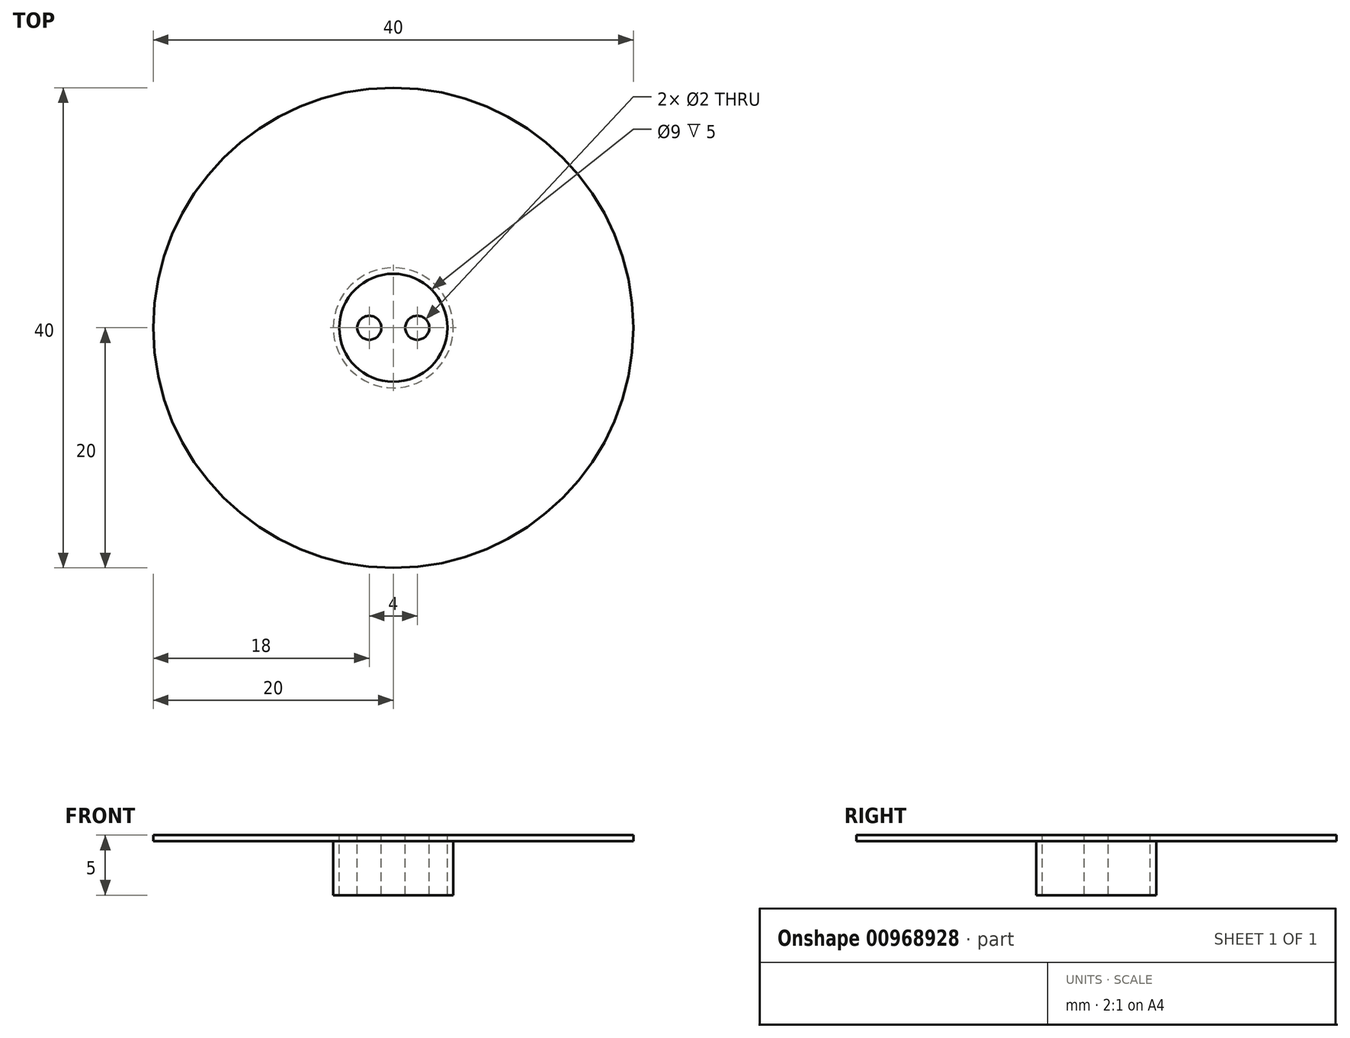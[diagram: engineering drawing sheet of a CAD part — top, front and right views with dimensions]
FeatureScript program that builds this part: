
annotation { "Feature Type Name" : "Feature", "Feature Type Description" : "" }
export const myFeature = defineFeature(function(context is Context, id is Id, definition is map)
    precondition{}
    {
        {
            var Q0;
            Q0=qCreatedBy(makeId("Top.planeOp"),FACE);
            var sketch = newSketch(context, id + "F0", { "sketchPlane" : qUnion([Q0])});
            skCircle(sketch, "E0", {"center": v(0, 0) * mm, "radius": 20 * mm});
            skSolve(sketch);
        }
        {
            var Q0;
            Q0=qSketchRegion(id+"F0",true);
            extrude(context, id + "F1", {"entities" : qUnion([Q0]), "depth" : 0.5 * mm, "offsetDistance" : 25 * mm});
        }
        {
            var Q0;
            Q0=makeQuery(id+"F1.opExtrude","CAP_FACE",FACE,{"disambiguationData":[OSD([sQuery(id+"F0.wireOp",EDGE,"E0")])],"isStart":false});
            var sketch = newSketch(context, id + "F2", { "sketchPlane" : qUnion([Q0])});
            skCircle(sketch, "E1", {"center": v(0, 0) * mm, "radius": 5 * mm});
            skSolve(sketch);
        }
        {
            var Q0;
            Q0=qSketchRegion(id+"F2",true);
            extrude(context, id + "F3", {"entities" : qUnion([Q0]), "operationType" : NewBodyOperationType.ADD, "oppositeDirection" : true, "depth" : 5 * mm, "offsetDistance" : 25 * mm});
        }
        {
            var Q0;
            Q0=makeQuery(id+"F1.opExtrude","CAP_FACE",FACE,{"disambiguationData":[OSD([sQuery(id+"F0.wireOp",EDGE,"E0")])],"isStart":false});
            var sketch = newSketch(context, id + "F4", { "sketchPlane" : qUnion([Q0])});
            skCircle(sketch, "E2", {"center": v(0, 0) * mm, "radius": 4.5 * mm});
            skSolve(sketch);
        }
        {
            var Q0;
            Q0=qSketchRegion(id+"F4",true);
            extrude(context, id + "F5", {"entities" : qUnion([Q0]), "operationType" : NewBodyOperationType.REMOVE, "oppositeDirection" : true, "depth" : 25 * mm, "offsetDistance" : 25 * mm});
        }
        {
            var Q0;
            Q0=makeQuery(id+"F1.opExtrude","CAP_FACE",FACE,{"disambiguationData":[OSD([sQuery(id+"F0.wireOp",EDGE,"E0")])],"isStart":false});
            var sketch = newSketch(context, id + "F6", { "sketchPlane" : qUnion([Q0])});
            skCircle(sketch, "E3", {"center": v(0, 0) * mm, "radius": 4.5 * mm});
            skSolve(sketch);
        }
        {
            var Q0;
            Q0=qSketchRegion(id+"F6",true);
            extrude(context, id + "F7", {"entities" : qUnion([Q0]), "oppositeDirection" : true, "depth" : 5 * mm, "offsetDistance" : 25 * mm});
        }
        {
            var Q0;
            Q0=makeQuery(id+"F7.opExtrude","CAP_FACE",FACE,{"disambiguationData":[OSD([sQuery(id+"F6.wireOp",EDGE,"E3")])],"isStart":true});
            var sketch = newSketch(context, id + "F8", { "sketchPlane" : qUnion([Q0])});
            skCircle(sketch, "E4", {"center": v(-2, 0) * mm, "radius": 1 * mm});
            skCircle(sketch, "E5", {"center": v(2, 0) * mm, "radius": 1 * mm});
            skSolve(sketch);
        }
        {
            var Q0;
            Q0=qSketchRegion(id+"F8",true);
            extrude(context, id + "F9", {"entities" : qUnion([Q0]), "oppositeDirection" : true, "depth" : 8 * mm, "offsetDistance" : 25 * mm});
        }
        {
            var Q0;
            Q0=makeQuery(id+"F9.opExtrude","CAP_FACE",FACE,{"disambiguationData":[OSD([sQuery(id+"F8.wireOp",EDGE,"E4")])],"isStart":false});
            var sketch = newSketch(context, id + "F10", { "sketchPlane" : qUnion([Q0])});
            skArc(sketch, "E6", {"start": v(-1, 0) * mm, "mid": v(-2, 1) * mm, "end": v(-3, 0) * mm});
            skArc(sketch, "E7", {"start": v(-2.75, 0) * mm, "mid": v(-2, -0.75) * mm, "end": v(-1.25, 0) * mm});
            skLineSegment(sketch, "E8", {"start": v(-3, 0) * mm, "end": v(-2.75, 0) * mm});
            skLineSegment(sketch, "E9", {"start": v(-1.25, 0) * mm, "end": v(-1, 0) * mm});
            skArc(sketch, "E10.1.0.0", {"start": v(3, 0) * mm, "mid": v(2, 1) * mm, "end": v(1, 0) * mm});
            skLineSegment(sketch, "E10.1.0.1", {"start": v(1, 0) * mm, "end": v(1.25, 0) * mm});
            skLineSegment(sketch, "E10.1.0.2", {"start": v(2.75, 0) * mm, "end": v(3, 0) * mm});
            skArc(sketch, "E10.1.0.3", {"start": v(1.25, 0) * mm, "mid": v(2, -0.75) * mm, "end": v(2.75, 0) * mm});
            skLineSegment(sketch, "E10.direction1", {"start": v(-3, 0) * mm, "end": v(1, 0) * mm, "construction": true});
            skSolve(sketch);
        }
        {
            var Q0;
            Q0=qSketchRegion(id+"F10",true);
            extrude(context, id + "F11", {"entities" : qUnion([Q0]), "operationType" : NewBodyOperationType.REMOVE, "oppositeDirection" : true, "depth" : 3 * mm, "offsetDistance" : 25 * mm});
        }
        {
            var Q0;
            Q0=makeQuery(id+"F7.opExtrude","CAP_FACE",FACE,{"disambiguationData":[OSD([sQuery(id+"F6.wireOp",EDGE,"E3")])],"isStart":true});
            var sketch = newSketch(context, id + "F12", { "sketchPlane" : qUnion([Q0])});
            skCircle(sketch, "E11", {"center": v(-2, 0) * mm, "radius": 1 * mm});
            skCircle(sketch, "E12", {"center": v(2, 0) * mm, "radius": 1 * mm});
            skSolve(sketch);
        }
        {
            var Q0;
            Q0 = qSketchRegion(id + "F12", true);
            extrude(context, id + "F13", {"entities" : qUnion([Q0]), "operationType" : NewBodyOperationType.REMOVE, "oppositeDirection" : true, "depth" : 25 * mm, "offsetDistance" : 25 * mm});
        }
    });
